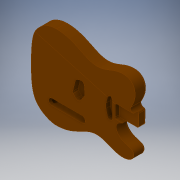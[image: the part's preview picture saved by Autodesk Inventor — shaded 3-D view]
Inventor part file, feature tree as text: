
AUTODESK INVENTOR PART (.ipt)
format: ipt  version: 2018 (Build 220112000, 112)  size: 697,856 bytes
history: native  units: in
note: dims shown in document units (in); Inventor stores cm internally (conversion verified against a paired STEP export)
features: sketch x13, other x6, projected_geometry x6, extrude x5, revolve x4, split x4, plane x2, hole x1, fillet x1
ambient origin geometry x8: Origin, YZ Plane, XZ Plane, XY Plane, X Axis, Y Axis, Z Axis, Center Point
bodies: Solid1 (feature_tree), body (feature_tree)
feature tree (42):
  sketch  "Sketch1"  dims[d10=14.3434in d17=7.0669in]
  extrude  "neck slot"  Depth=7.0669in
  extrude  "bridge pickup cavity"  Depth=9.3158in
  extrude  "neck pickup cavity"  Depth=0.1969in
  sketch  "Sketch11"  dims[d35=0.25in d36=3.002in]
  extrude  "control cavity"  Depth=1.6929in
  extrude  "back cavity"  Depth=0.25in
  hole  "arduino mount holes"  [1 undecoded]
  other  "Bridge Mount Screw Hole Datum"
  other  "Bridge Pickup to Control Hole Plane"
  revolve  "Revolution1"  [1 undecoded]
  other  "Bridge Pickup to Back Cavity Hole Plane"
  split  "Split1"
  revolve  "Revolution2"  [1 undecoded]
  sketch  "Sketch17"  dims[d77=0.687in d78=0.0in]
  plane  "Work Plane6"
  split  "Split2"
  revolve  "Revolution3"  [1 undecoded]
  plane  "Work Plane7"
  split  "Split3"
  revolve  "Revolution4"  [1 undecoded]
  split  "Split4"
  fillet  "Fillet1"  Radius=0.715in
  other  "Image1"
  sketch  "Sketch2"  dims[d24=7.4596in d25=9.3158in]
  sketch  "Sketch3"  dims[d26=0.1969in d27=0.1969in]
  projected_geometry  "Projected Loop1"
  sketch  "Sketch6"  dims[d28=0.4331in d31=1.6929in]
  sketch  "Sketch9"  dims[d32=1.75in d33=0.0in d34=0.25in]
  projected_geometry  "Projected Loop4"
  projected_geometry  "Projected Loop5"
  sketch  "Sketch12"  dims[d37=0.625in d38=0.0in d54=0.85in d55=0.0in]
  sketch  "Sketch13"  dims[d69=2.135in d70=3.002in]
  projected_geometry  "Projected Loop7"
  sketch  "Sketch15"  dims[d72=0.343in d73=0.4315in]
  projected_geometry  "Projected Loop8"
  sketch  "Sketch16"  dims[d74=0.617in d75=2.564in d76=0.715in]
  other  "Work Axis3"
  sketch  "Sketch18"  dims[d79=7.37in]
  projected_geometry  "Projected Loop11"
  other  "Work Axis4"
  sketch  "Sketch19"  dims[d80=0.265in d81=0.43in d82=2.222in d83=1.71in d84=1.577in d85=1.025in d87=0.134in d88=2.495in d89=0.982in d97=1.0in d98=4.57in d99=5.06in d100=3.125in d101=1.5in d102=0.0in d107=0.25in d108=2.3622in d109=6.2992in d110=2.1654in d111=4.9213in d112=0.9843in d113=0.0in d114=0.6982in d117=0.25in d119=6.378in d120=8.9472in d121=6.3764in d122=9.058in d123=12.7966in d125=1.9in d126=2.95in d127=3.25in d128=0.2362in d129=0.0787in d130=0.2362in d131=0.119in d132=0.0787in d133=0.5635in d134=0.1969in d135=0.8108in d137=-7.37in d138=1.71in d139=0.125in d140=0.125in d141=0.1969in d142=0.1969in d143=90.0deg d144=1.7717in d145=0.125in d146=0.125in d147=0.0787in d148=0.0787in d149=90.0deg d151=0.1969in d153=0.125in d154=0.125in d155=0.1969in d156=90.0deg d157=135.0deg d159=0.875in d160=0.875in d161=90.0deg d162=0.2362in]
note: 5 required parameter values undecoded (feature->parameter linkage not recoverable at this tier; creation-order binding heuristic only, values carry confidence <= 0.55)